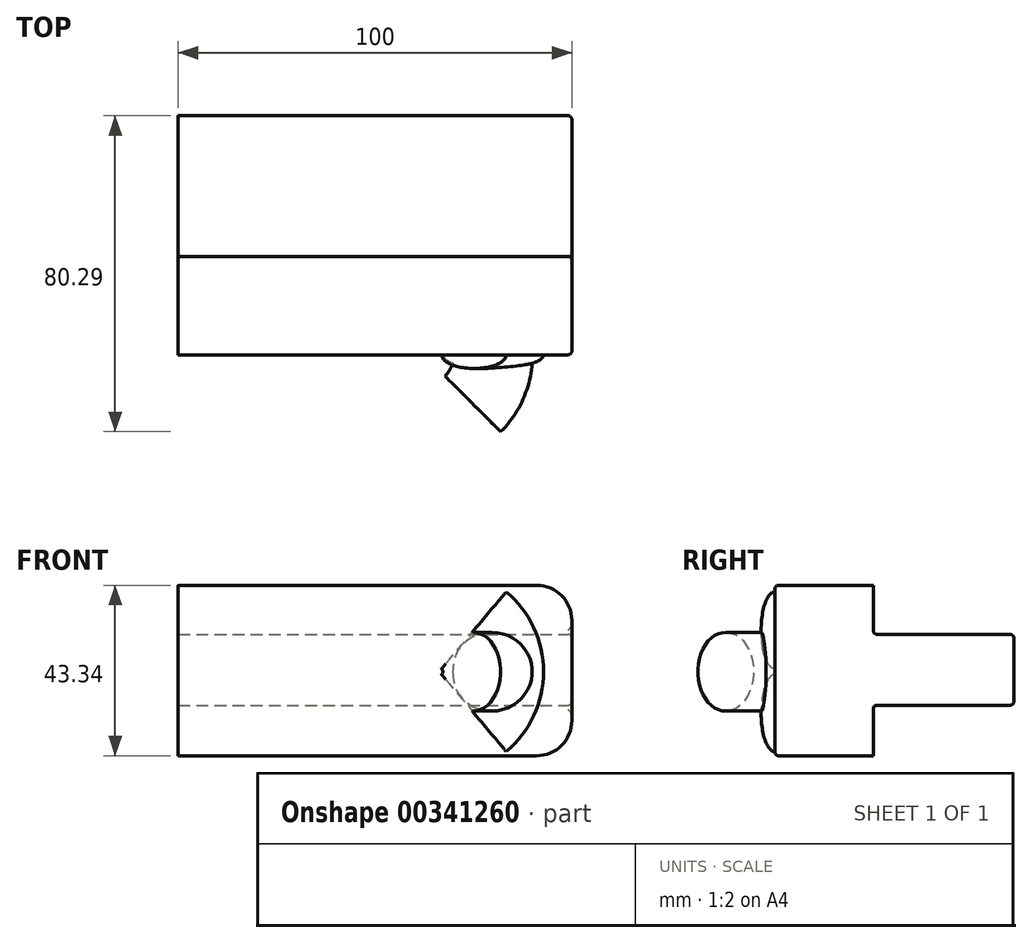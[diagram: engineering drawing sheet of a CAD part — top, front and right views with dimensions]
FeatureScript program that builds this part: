
annotation { "Feature Type Name" : "Feature", "Feature Type Description" : "" }
export const myFeature = defineFeature(function(context is Context, id is Id, definition is map)
    precondition{}
    {
        {
            var Q0;
            Q0=qCreatedBy(makeId("Front.planeOp"),FACE);
            var sketch = newSketch(context, id + "F0", { "sketchPlane" : qUnion([Q0])});
            skCircle(sketch, "E0", {"center": v(0, 0) * mm, "radius": 10 * mm});
            skSolve(sketch);
        }
        {
            var Q0;
            Q0=qCreatedBy(makeId("Front.planeOp"),FACE);
            var sketch = newSketch(context, id + "F1", { "sketchPlane" : qUnion([Q0])});
            skLineSegment(sketch, "E1", {"start": v(-17.65, 8.88) * mm, "end": v(-17.65, -11.04) * mm});
            skSolve(sketch);
        }
        {
            var Q0;
            Q0=makeQuery(id+"F0.imprint","IMPRINT",FACE,{"disambiguationData":[TD([[makeQuery(id+"F0.imprint","IMPRINT",EDGE,{"derivedFrom":sQuery(id+"F0.wireOp",EDGE,"E0")}),1.0]])]});
            var Q1;
            Q1=sQuery(id+"F1.wireOp",EDGE,"E1");
            revolve(context, id + "F2", {"entities" : qUnion([Q0]), "axis" : qUnion([Q1]), "revolveType" : RevolveType.TWO_DIRECTIONS, "angle" : 45 * degree, "angleBack" : 270 * degree});
        }
        {
            var Q0;
            Q0=qCreatedBy(makeId("Top.planeOp"),FACE);
            var sketch = newSketch(context, id + "F3", { "sketchPlane" : qUnion([Q0])});
            skEllipse(sketch, "E2", {"center": v(0, 0) * mm, "majorRadius": 12.78 * mm, "minorRadius": 3.48 * mm, "majorAxis": v(1, 0)});
            skSolve(sketch);
        }
        {
            var Q0;
            Q0=qCreatedBy(makeId("Top.planeOp"),FACE);
            var sketch = newSketch(context, id + "F4", { "sketchPlane" : qUnion([Q0])});
            skLineSegment(sketch, "E3", {"start": v(-13.72, -2.71) * mm, "end": v(-13.72, 2.44) * mm});
            skSolve(sketch);
        }
        {
            var Q0;
            Q0=makeQuery(id+"F3.imprint","IMPRINT",FACE,{"disambiguationData":[TD([[makeQuery(id+"F3.imprint","IMPRINT",EDGE,{"derivedFrom":sQuery(id+"F3.wireOp",EDGE,"E2")}),1.0]])]});
            var Q1;
            Q1=sQuery(id+"F4.wireOp",EDGE,"E3");
            revolve(context, id + "F5", {"operationType" : NewBodyOperationType.ADD, "entities" : qUnion([Q0]), "axis" : qUnion([Q1]), "revolveType" : RevolveType.SYMMETRIC, "angle" : 100 * degree});
        }
        {
            var Q0;
            Q0=qCreatedBy(makeId("Right.planeOp"),FACE);
            var sketch = newSketch(context, id + "F6", { "sketchPlane" : qUnion([Q0])});
            skLineSegment(sketch, "E4.bottom", {"start": v(0, 21.97) * mm, "end": v(25, 21.97) * mm});
            skLineSegment(sketch, "E4.top", {"start": v(0, -21.37) * mm, "end": v(25, -21.37) * mm});
            skLineSegment(sketch, "E4.left", {"start": v(0, 21.97) * mm, "end": v(0, -21.37) * mm});
            skLineSegment(sketch, "E4.right", {"start": v(25, 21.97) * mm, "end": v(25, -21.37) * mm});
            skSolve(sketch);
        }
        {
            var Q0;
            Q0=makeQuery(id+"F6.imprint","IMPRINT",FACE,{"disambiguationData":[TD([[makeQuery(id+"F6.imprint","IMPRINT",EDGE,{"derivedFrom":sQuery(id+"F6.wireOp",EDGE,"E4.bottom")}),-1.0]])]});
            extrude(context, id + "F7", {"entities" : qUnion([Q0]), "operationType" : NewBodyOperationType.ADD, "oppositeDirection" : true, "depth" : 80 * mm, "hasSecondDirection" : true, "secondDirectionOppositeDirection" : false, "secondDirectionDepth" : 20 * mm});
        }
        {
            var Q0;
            Q0=qCreatedBy(makeId("Right.planeOp"),FACE);
            var sketch = newSketch(context, id + "F8", { "sketchPlane" : qUnion([Q0])});
            skLineSegment(sketch, "E5.bottom", {"start": v(22.33, 9.48) * mm, "end": v(60.74, 9.48) * mm});
            skLineSegment(sketch, "E5.top", {"start": v(22.33, -8.52) * mm, "end": v(60.74, -8.52) * mm});
            skLineSegment(sketch, "E5.left", {"start": v(22.33, 9.48) * mm, "end": v(22.33, -8.52) * mm});
            skLineSegment(sketch, "E5.right", {"start": v(60.74, 9.48) * mm, "end": v(60.74, -8.52) * mm});
            skSolve(sketch);
        }
        {
            var Q0;
            Q0=makeQuery(id+"F8.imprint","IMPRINT",FACE,{"disambiguationData":[TD([[makeQuery(id+"F8.imprint","IMPRINT",EDGE,{"derivedFrom":sQuery(id+"F8.wireOp",EDGE,"E5.bottom")}),-1.0]])]});
            extrude(context, id + "F9", {"entities" : qUnion([Q0]), "operationType" : NewBodyOperationType.ADD, "oppositeDirection" : true, "depth" : 80 * mm, "hasSecondDirection" : true, "secondDirectionOppositeDirection" : false, "secondDirectionDepth" : 20 * mm});
        }
        {
            var Q0;
            Q0=makeQuery(id+"F7.opExtrude","SWEPT_EDGE",EDGE,{"disambiguationData":[OSD([sQuery(id+"F6.wireOp",EDGE,"E4.top"),sQuery(id+"F6.wireOp",EDGE,"E4.left")])]});
            var Q1;
            Q1=makeQuery(id+"F7.opExtrude","CAP_EDGE",EDGE,{"disambiguationData":[OSD([sQuery(id+"F6.wireOp",EDGE,"E4.left")])],"isStart":true});
            var Q2;
            Q2=makeQuery(id+"F7.opExtrude","SWEPT_EDGE",EDGE,{"disambiguationData":[OSD([sQuery(id+"F6.wireOp",EDGE,"E4.bottom"),sQuery(id+"F6.wireOp",EDGE,"E4.left")])]});
            var Q3;
            Q3=makeQuery(id+"F9.opExtrude","SWEPT_EDGE",EDGE,{"disambiguationData":[OSD([sQuery(id+"F8.wireOp",EDGE,"E5.bottom"),sQuery(id+"F8.wireOp",EDGE,"E5.right")])]});
            var Q4;
            Q4=makeQuery(id+"F9.opExtrude","CAP_EDGE",EDGE,{"disambiguationData":[OSD([sQuery(id+"F8.wireOp",EDGE,"E5.bottom")])],"isStart":true});
            var Q5;
            Q5=makeQuery(id+"F9.opExtrude","CAP_EDGE",EDGE,{"disambiguationData":[OSD([sQuery(id+"F8.wireOp",EDGE,"E5.top")])],"isStart":true});
            var Q6;
            Q6=makeQuery(id+"F9.opExtrude","CAP_EDGE",EDGE,{"disambiguationData":[OSD([sQuery(id+"F8.wireOp",EDGE,"E5.right")])],"isStart":true});
            var Q7;
            Q7=makeQuery(id+"F9.boolean.opBoolean","INTERSECT",EDGE,{"derivedFrom":[makeQuery(id+"F7.opExtrude","SWEPT_FACE",FACE,{"disambiguationData":[OSD([sQuery(id+"F6.wireOp",EDGE,"E4.right")])]}),makeQuery(id+"F9.opExtrude","SWEPT_FACE",FACE,{"disambiguationData":[OSD([sQuery(id+"F8.wireOp",EDGE,"E5.top")])]})]});
            var Q8;
            Q8=makeQuery(id+"F9.opExtrude","SWEPT_EDGE",EDGE,{"disambiguationData":[OSD([sQuery(id+"F8.wireOp",EDGE,"E5.top"),sQuery(id+"F8.wireOp",EDGE,"E5.right")])]});
            var Q9;
            Q9=makeQuery(id+"F9.boolean.opBoolean","INTERSECT",EDGE,{"derivedFrom":[makeQuery(id+"F7.opExtrude","SWEPT_FACE",FACE,{"disambiguationData":[OSD([sQuery(id+"F6.wireOp",EDGE,"E4.right")])]}),makeQuery(id+"F9.opExtrude","SWEPT_FACE",FACE,{"disambiguationData":[OSD([sQuery(id+"F8.wireOp",EDGE,"E5.bottom")])]})]});
            fillet(context, id + "F10", {"entities" : qUnion([Q0, Q1, Q2, Q3, Q4, Q5, Q6, Q7, Q8, Q9]), "radius" : 1 * mm, "tangentPropagation" : true, "allowEdgeOverflow" : false});
        }
        {
            var Q0;
            Q0=makeQuery(id+"F7.opExtrude","CAP_EDGE",EDGE,{"disambiguationData":[OSD([sQuery(id+"F6.wireOp",EDGE,"E4.top")])],"isStart":true});
            var Q1;
            Q1=makeQuery(id+"F7.opExtrude","CAP_EDGE",EDGE,{"disambiguationData":[OSD([sQuery(id+"F6.wireOp",EDGE,"E4.bottom")])],"isStart":true});
            fillet(context, id + "F11", {"entities" : qUnion([Q0, Q1]), "radius" : 9 * mm, "tangentPropagation" : true, "allowEdgeOverflow" : false});
        }
    });
